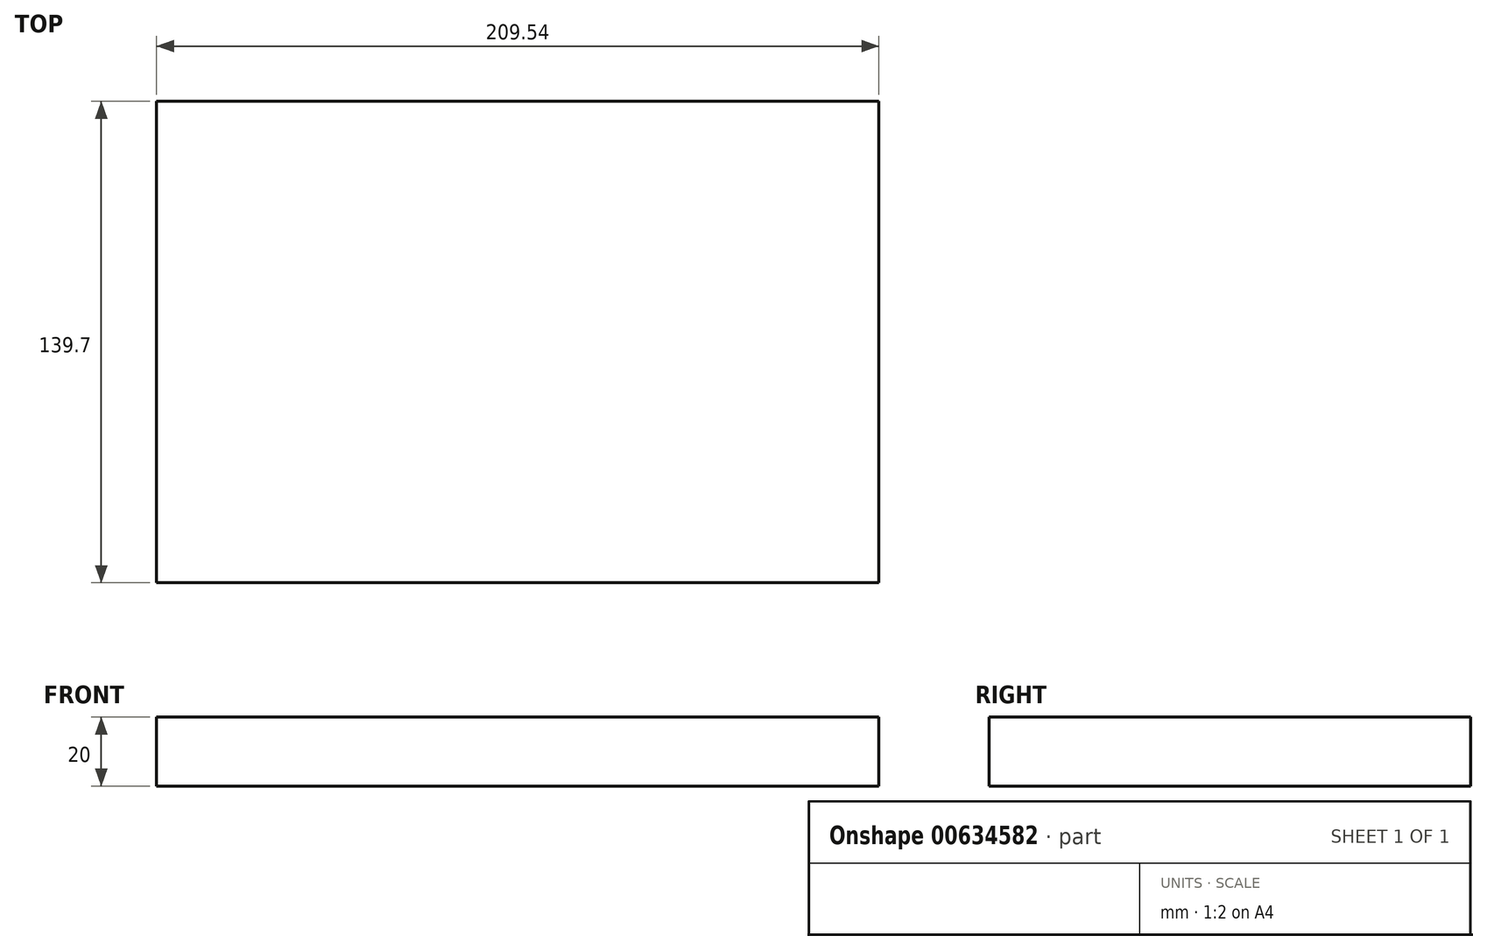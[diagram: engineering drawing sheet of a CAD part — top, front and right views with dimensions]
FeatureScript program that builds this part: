
annotation { "Feature Type Name" : "Feature", "Feature Type Description" : "" }
export const myFeature = defineFeature(function(context is Context, id is Id, definition is map)
    precondition{}
    {
        {
            var Q0;
            Q0=qCreatedBy(makeId("Top.planeOp"),FACE);
            var sketch = newSketch(context, id + "F0", { "sketchPlane" : qUnion([Q0])});
            skLineSegment(sketch, "E0.bottom", {"start": v(104.78, -69.85) * mm, "end": v(-104.78, -69.85) * mm});
            skLineSegment(sketch, "E0.top", {"start": v(104.78, 69.85) * mm, "end": v(-104.78, 69.85) * mm});
            skLineSegment(sketch, "E0.left", {"start": v(104.78, -69.85) * mm, "end": v(104.78, 69.85) * mm});
            skLineSegment(sketch, "E0.right", {"start": v(-104.78, -69.85) * mm, "end": v(-104.78, 69.85) * mm});
            skPoint(sketch, "E0.middle", {"position": v(0, 0) * mm});
            skSolve(sketch);
        }
        {
            var Q0;
            Q0 = qSketchRegion(id + "F0", true);
            extrude(context, id + "F1", {"entities" : qUnion([Q0]), "depth" : 20 * mm, "offsetDistance" : 25.4 * mm});
        }
    });
